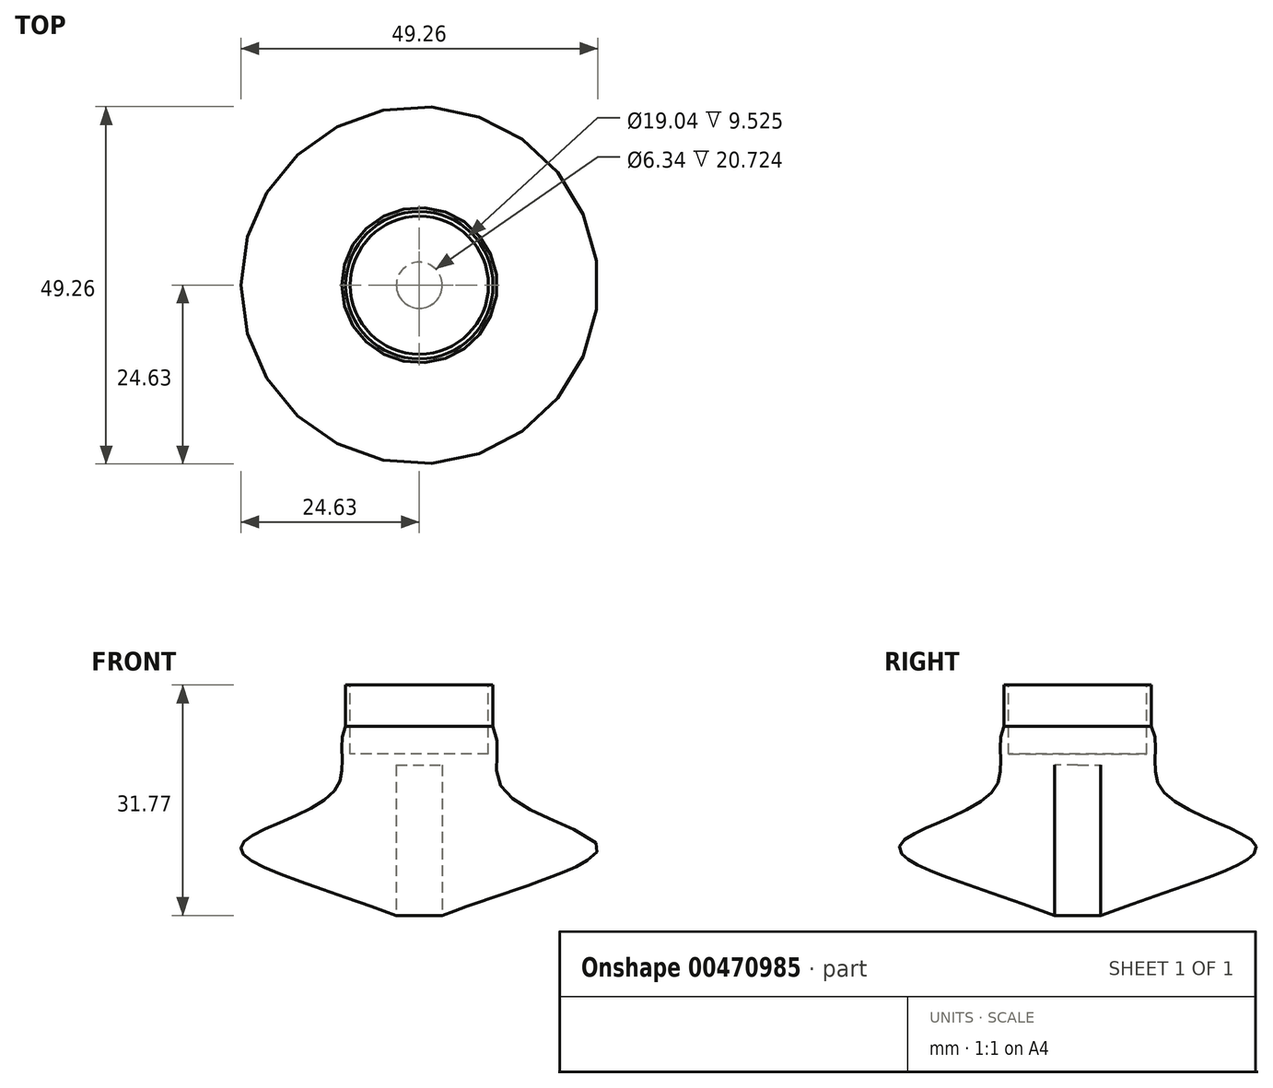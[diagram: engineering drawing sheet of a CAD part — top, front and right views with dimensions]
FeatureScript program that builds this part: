
annotation { "Feature Type Name" : "Feature", "Feature Type Description" : "" }
export const myFeature = defineFeature(function(context is Context, id is Id, definition is map)
    precondition{}
    {
        {
            var Q0;
            Q0=qCreatedBy(makeId("Front.planeOp"),FACE);
            var sketch = newSketch(context, id + "F0", { "sketchPlane" : qUnion([Q0])});
            skLineSegment(sketch, "E0", {"start": v(0, 0) * mm, "end": v(0, 33.02) * mm});
            skFitSpline(sketch, "E1", {"points": [v(0, 33.02) * mm, v(10.16, 27.35) * mm, v(11.67, 18.45) * mm, v(24.56, 10.88) * mm, v(0, 0) * mm], "startDerivative": vector(36.31, 3.17) * mm, "endDerivative": vector(-103.93, -42.74) * mm});
            skLineSegment(sketch, "E2", {"start": v(0, 33.02) * mm, "end": v(10.16, 33.02) * mm});
            skLineSegment(sketch, "E3", {"start": v(10.16, 33.02) * mm, "end": v(10.16, 27.35) * mm});
            skSolve(sketch);
        }
        {
            var Q0;
            Q0=makeQuery(id+"F0.imprint","IMPRINT",FACE,{"disambiguationData":[TD([[makeQuery(id+"F0.imprint","IMPRINT",EDGE,{"derivedFrom":sQuery(id+"F0.wireOp",EDGE,"E0")}),-1.0]])]});
            var Q1;
            {var subQ0=sQuery(id+"F0.wireOp",EDGE,"E3");Q1=makeQuery(id+"F0.imprint","IMPRINT",FACE,{"disambiguationData":[TD([[makeQuery(id+"F0.imprint","IMPRINT",EDGE,{"derivedFrom":subQ0}),-1.0]])]});}
            var Q2;
            Q2=sQuery(id+"F0.wireOp",EDGE,"E0");
            revolve(context, id + "F1", {"entities" : qUnion([Q0, Q1]), "axis" : qUnion([Q2]), "revolveType" : RevolveType.FULL});
        }
        {
            var Q0;
            Q0=makeQuery(id+"F1.opRevolve","SWEPT_FACE",FACE,{"disambiguationData":[OSD([sQuery(id+"F0.wireOp",EDGE,"E2")])]});
            var sketch = newSketch(context, id + "F2", { "sketchPlane" : qUnion([Q0])});
            skCircle(sketch, "E4", {"center": v(0, 0) * mm, "radius": 9.52 * mm});
            skSolve(sketch);
        }
        {
            var Q0;
            Q0=makeQuery(id+"F2.imprint","IMPRINT",FACE,{"disambiguationData":[TD([[makeQuery(id+"F2.imprint","IMPRINT",EDGE,{"derivedFrom":sQuery(id+"F2.wireOp",EDGE,"E4")}),1.0]])]});
            extrude(context, id + "F3", {"entities" : qUnion([Q0]), "operationType" : NewBodyOperationType.REMOVE, "oppositeDirection" : true, "depth" : 9.52 * mm});
        }
        {
            var Q0;
            Q0=qCreatedBy(makeId("Top.planeOp"),FACE);
            var sketch = newSketch(context, id + "F4", { "sketchPlane" : qUnion([Q0])});
            skCircle(sketch, "E5", {"center": v(0, 0) * mm, "radius": 3.17 * mm});
            skSolve(sketch);
        }
        {
            var Q0;
            Q0=makeQuery(id+"F4.imprint","IMPRINT",FACE,{"disambiguationData":[TD([[makeQuery(id+"F4.imprint","IMPRINT",EDGE,{"derivedFrom":sQuery(id+"F4.wireOp",EDGE,"E5")}),1.0]])]});
            extrude(context, id + "F5", {"entities" : qUnion([Q0]), "operationType" : NewBodyOperationType.REMOVE, "depth" : 21.97 * mm});
        }
    });
